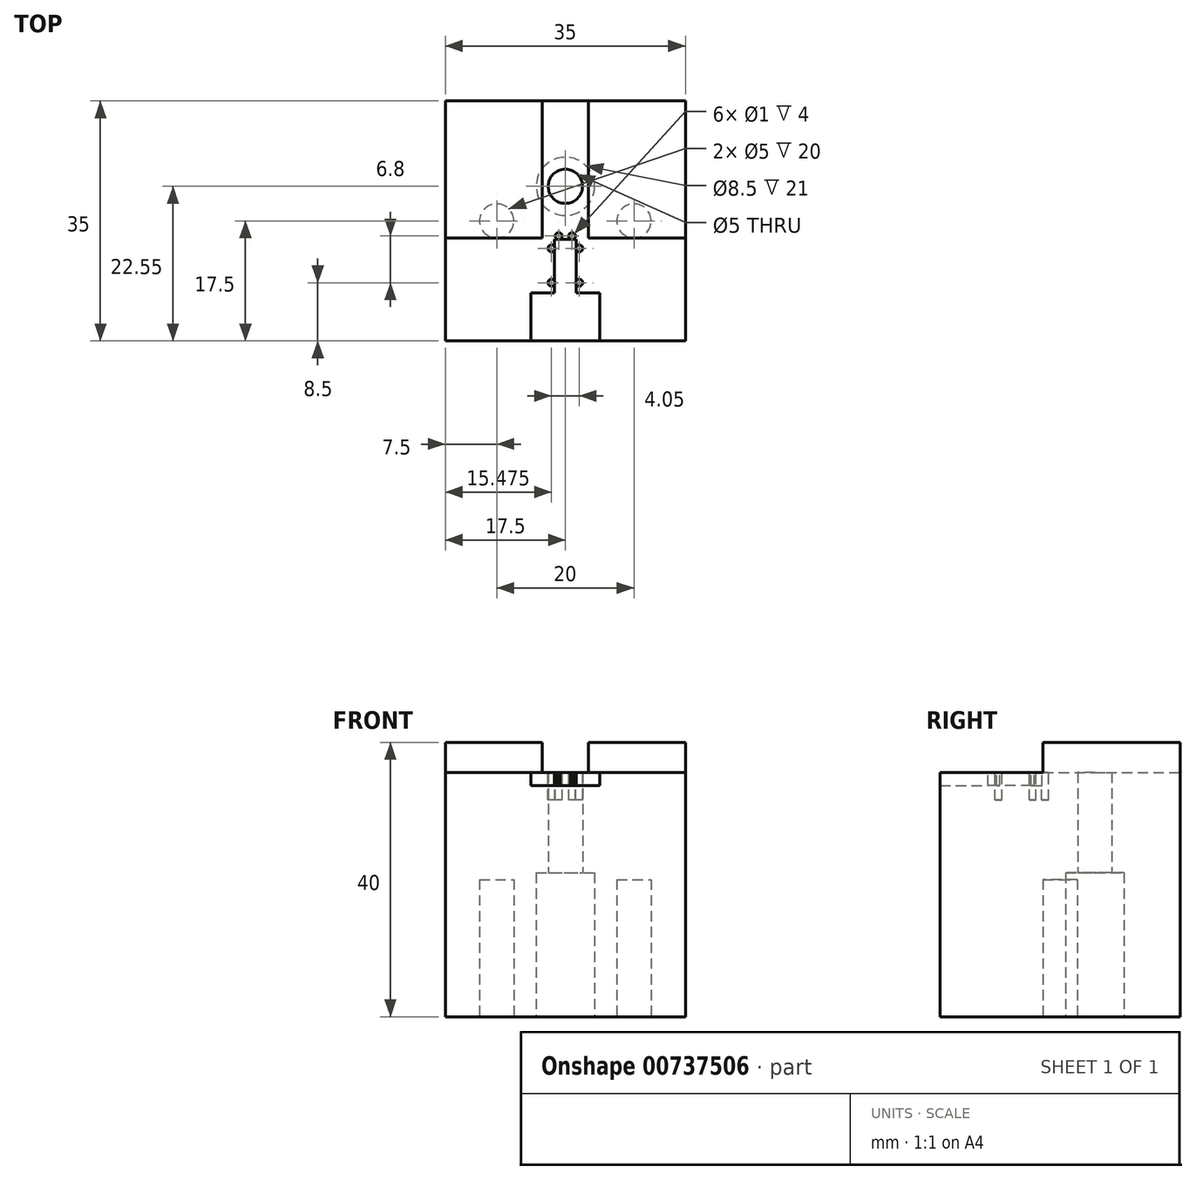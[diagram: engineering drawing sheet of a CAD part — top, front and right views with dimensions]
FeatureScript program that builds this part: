
annotation { "Feature Type Name" : "Feature", "Feature Type Description" : "" }
export const myFeature = defineFeature(function(context is Context, id is Id, definition is map)
    precondition{}
    {
        {
            var Q0;
            Q0=qCreatedBy(makeId("Top.planeOp"),FACE);
            var sketch = newSketch(context, id + "F0", { "sketchPlane" : qUnion([Q0])});
            skLineSegment(sketch, "E0.bottom", {"start": v(-17.5, 17.5) * mm, "end": v(17.5, 17.5) * mm});
            skLineSegment(sketch, "E0.top", {"start": v(-17.5, -17.5) * mm, "end": v(17.5, -17.5) * mm});
            skLineSegment(sketch, "E0.left", {"start": v(-17.5, 17.5) * mm, "end": v(-17.5, -17.5) * mm});
            skLineSegment(sketch, "E0.right", {"start": v(17.5, 17.5) * mm, "end": v(17.5, -17.5) * mm});
            skLineSegment(sketch, "E1", {"start": v(-17.5, 17.5) * mm, "end": v(17.5, -17.5) * mm, "construction": true});
            skSolve(sketch);
        }
        {
            var Q0;
            Q0 = qSketchRegion(id + "F0", true);
            extrude(context, id + "F1", {"entities" : qUnion([Q0]), "depth" : 40 * mm, "offsetDistance" : 25 * mm});
        }
        {
            var Q0;
            Q0=makeQuery(id+"F1.opExtrude","CAP_FACE",FACE,{"disambiguationData":[OSD([sQuery(id+"F0.wireOp",EDGE,"E0.bottom"),sQuery(id+"F0.wireOp",EDGE,"E0.top"),sQuery(id+"F0.wireOp",EDGE,"E0.left"),sQuery(id+"F0.wireOp",EDGE,"E0.right")])],"isStart":true});
            var sketch = newSketch(context, id + "F2", { "sketchPlane" : qUnion([Q0])});
            skCircle(sketch, "E2", {"center": v(-10, 0) * mm, "radius": 2.5 * mm});
            skCircle(sketch, "E3", {"center": v(10, 0) * mm, "radius": 2.5 * mm});
            skSolve(sketch);
        }
        {
            var Q0;
            Q0 = qSketchRegion(id + "F2", true);
            extrude(context, id + "F3", {"entities" : qUnion([Q0]), "operationType" : NewBodyOperationType.REMOVE, "oppositeDirection" : true, "depth" : 20 * mm, "offsetDistance" : 25 * mm});
        }
        {
            var Q0;
            Q0=makeQuery(id+"F1.opExtrude","CAP_FACE",FACE,{"disambiguationData":[OSD([sQuery(id+"F0.wireOp",EDGE,"E0.bottom"),sQuery(id+"F0.wireOp",EDGE,"E0.top"),sQuery(id+"F0.wireOp",EDGE,"E0.left"),sQuery(id+"F0.wireOp",EDGE,"E0.right")])],"isStart":false});
            var sketch = newSketch(context, id + "F4", { "sketchPlane" : qUnion([Q0])});
            skLineSegment(sketch, "E4.bottom", {"start": v(17.5, -17.5) * mm, "end": v(-17.5, -17.5) * mm});
            skLineSegment(sketch, "E4.top", {"start": v(17.5, -2.5) * mm, "end": v(3.35, -2.5) * mm});
            skLineSegment(sketch, "E4.left", {"start": v(17.5, -17.5) * mm, "end": v(17.5, -2.5) * mm});
            skLineSegment(sketch, "E4.right", {"start": v(-17.5, -17.5) * mm, "end": v(-17.5, -2.5) * mm});
            skLineSegment(sketch, "E5", {"start": v(-3.35, -2.5) * mm, "end": v(-3.35, 17.5) * mm});
            skLineSegment(sketch, "E6", {"start": v(3.35, -2.5) * mm, "end": v(3.35, 17.5) * mm});
            skLineSegment(sketch, "E7.trimOffspring", {"start": v(-3.35, -2.5) * mm, "end": v(-17.5, -2.5) * mm});
            skSolve(sketch);
        }
        {
            var Q0;
            Q0 = qSketchRegion(id + "F4", true);
            var Q1;
            Q1=makeQuery(id+"F4.imprint","IMPRINT",FACE,{"disambiguationData":[TD([[makeQuery(id+"F4.imprint","IMPRINT",EDGE,{"derivedFrom":sQuery(id+"F4.wireOp",EDGE,"E4.bottom")}),1.0]])]});
            extrude(context, id + "F5", {"entities" : qUnion([Q0, Q1]), "operationType" : NewBodyOperationType.REMOVE, "oppositeDirection" : true, "depth" : 4.4 * mm, "offsetDistance" : 25 * mm});
        }
        {
            var Q0;
            Q0=makeQuery(id+"F1.opExtrude","CAP_FACE",FACE,{"disambiguationData":[OSD([sQuery(id+"F0.wireOp",EDGE,"E0.bottom"),sQuery(id+"F0.wireOp",EDGE,"E0.top"),sQuery(id+"F0.wireOp",EDGE,"E0.left"),sQuery(id+"F0.wireOp",EDGE,"E0.right")])],"isStart":true});
            var sketch = newSketch(context, id + "F6", { "sketchPlane" : qUnion([Q0])});
            skCircle(sketch, "E8", {"center": v(0, -5.05) * mm, "radius": 4.25 * mm});
            skSolve(sketch);
        }
        {
            var Q0;
            Q0 = qSketchRegion(id + "F6", true);
            extrude(context, id + "F7", {"entities" : qUnion([Q0]), "operationType" : NewBodyOperationType.REMOVE, "oppositeDirection" : true, "depth" : 21 * mm, "offsetDistance" : 25 * mm});
        }
        {
            var Q0;
            Q0=makeQuery(id+"F7.boolean.opBoolean","COPY",FACE,{"derivedFrom":makeQuery(id+"F7.opExtrude","CAP_FACE",FACE,{"disambiguationData":[OSD([sQuery(id+"F6.wireOp",EDGE,"E8")])],"isStart":false})});
            var sketch = newSketch(context, id + "F8", { "sketchPlane" : qUnion([Q0])});
            skCircle(sketch, "E9", {"center": v(0, -5.05) * mm, "radius": 2.5 * mm});
            skSolve(sketch);
        }
        {
            var Q0;
            Q0 = qSketchRegion(id + "F8", true);
            extrude(context, id + "F9", {"entities" : qUnion([Q0]), "operationType" : NewBodyOperationType.REMOVE, "endBound" : BoundingType.UP_TO_NEXT, "oppositeDirection" : true, "depth" : 25 * mm, "offsetDistance" : 25 * mm});
        }
        {
            var Q0;
            Q0=makeQuery(id+"F5.boolean.opBoolean","COPY",FACE,{"derivedFrom":makeQuery(id+"F5.opExtrude","CAP_FACE",FACE,{"disambiguationData":[OSD([sQuery(id+"F0.wireOp",EDGE,"E0.bottom"),sQuery(id+"F4.wireOp",EDGE,"E4.bottom"),sQuery(id+"F4.wireOp",EDGE,"E4.top"),sQuery(id+"F4.wireOp",EDGE,"E4.left"),sQuery(id+"F4.wireOp",EDGE,"E4.right"),sQuery(id+"F4.wireOp",EDGE,"E5"),sQuery(id+"F4.wireOp",EDGE,"E6"),sQuery(id+"F4.wireOp",EDGE,"E7.trimOffspring")])],"isStart":false})});
            var sketch = newSketch(context, id + "F10", { "sketchPlane" : qUnion([Q0])});
            skLineSegment(sketch, "E10.bottom", {"start": v(5, -17.5) * mm, "end": v(-5, -17.5) * mm});
            skLineSegment(sketch, "E10.top", {"start": v(5, -10.5) * mm, "end": v(1.58, -10.5) * mm});
            skLineSegment(sketch, "E10.left", {"start": v(5, -17.5) * mm, "end": v(5, -10.5) * mm});
            skLineSegment(sketch, "E10.right", {"start": v(-5, -17.5) * mm, "end": v(-5, -10.5) * mm});
            skLineSegment(sketch, "E11", {"start": v(-1.57, -10.5) * mm, "end": v(-1.57, -2.65) * mm});
            skLineSegment(sketch, "E12", {"start": v(-1.57, -2.65) * mm, "end": v(1.58, -2.65) * mm});
            skLineSegment(sketch, "E13", {"start": v(1.58, -2.65) * mm, "end": v(1.58, -10.5) * mm});
            skLineSegment(sketch, "E14.trimOffspring", {"start": v(-1.57, -10.5) * mm, "end": v(-5, -10.5) * mm});
            skSolve(sketch);
        }
        {
            var Q0;
            Q0 = qSketchRegion(id + "F10", true);
            extrude(context, id + "F11", {"entities" : qUnion([Q0]), "operationType" : NewBodyOperationType.REMOVE, "oppositeDirection" : true, "depth" : 1.9 * mm, "offsetDistance" : 25 * mm});
        }
        {
            var Q0;
            Q0=makeQuery(id+"F5.boolean.opBoolean","COPY",FACE,{"derivedFrom":makeQuery(id+"F5.opExtrude","CAP_FACE",FACE,{"disambiguationData":[OSD([sQuery(id+"F0.wireOp",EDGE,"E0.bottom"),sQuery(id+"F4.wireOp",EDGE,"E4.bottom"),sQuery(id+"F4.wireOp",EDGE,"E4.top"),sQuery(id+"F4.wireOp",EDGE,"E4.left"),sQuery(id+"F4.wireOp",EDGE,"E4.right"),sQuery(id+"F4.wireOp",EDGE,"E5"),sQuery(id+"F4.wireOp",EDGE,"E6"),sQuery(id+"F4.wireOp",EDGE,"E7.trimOffspring")])],"isStart":false})});
            var sketch = newSketch(context, id + "F12", { "sketchPlane" : qUnion([Q0])});
            skCircle(sketch, "E15", {"center": v(-2.02, -9) * mm, "radius": 0.5 * mm});
            skCircle(sketch, "E16", {"center": v(-2.02, -4) * mm, "radius": 0.5 * mm});
            skCircle(sketch, "E17.MirrorC", {"center": v(2.02, -9) * mm, "radius": 0.5 * mm});
            skCircle(sketch, "E18.MirrorC", {"center": v(2.02, -4) * mm, "radius": 0.5 * mm});
            skCircle(sketch, "E19", {"center": v(-0.97, -2.2) * mm, "radius": 0.5 * mm});
            skCircle(sketch, "E20", {"center": v(0.98, -2.2) * mm, "radius": 0.5 * mm});
            skSolve(sketch);
        }
        {
            var Q0;
            Q0 = qSketchRegion(id + "F12", true);
            extrude(context, id + "F13", {"entities" : qUnion([Q0]), "operationType" : NewBodyOperationType.REMOVE, "oppositeDirection" : true, "depth" : 4 * mm, "offsetDistance" : 25 * mm});
        }
    });
